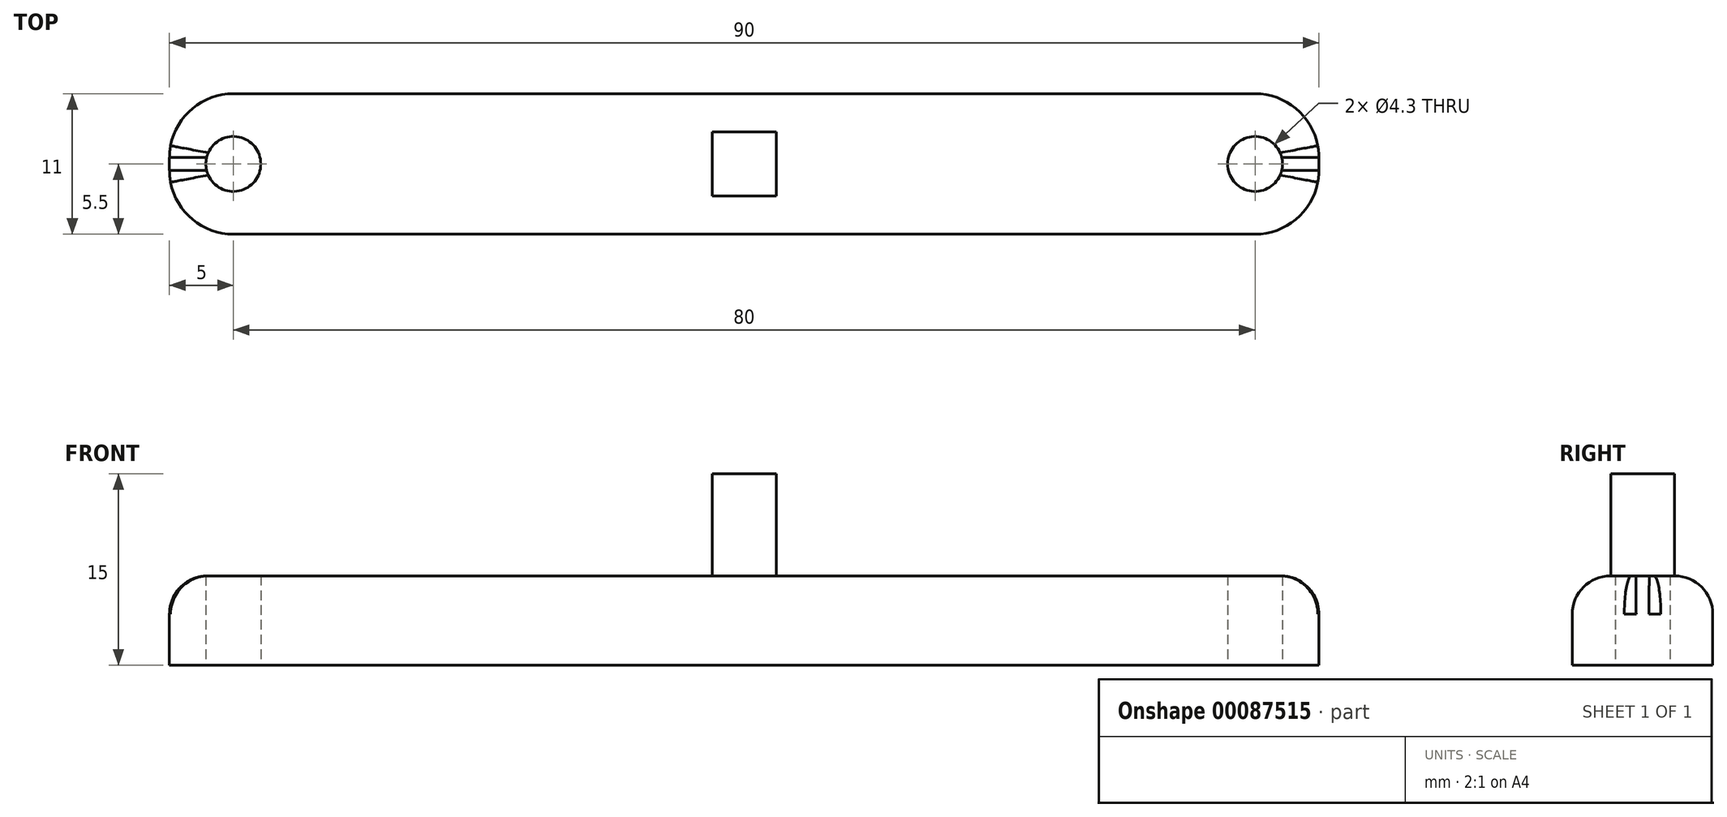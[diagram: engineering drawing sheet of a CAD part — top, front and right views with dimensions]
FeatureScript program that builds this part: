
annotation { "Feature Type Name" : "Feature", "Feature Type Description" : "" }
export const myFeature = defineFeature(function(context is Context, id is Id, definition is map)
    precondition{}
    {
        {
            var Q0;
            Q0=qCreatedBy(makeId("Top.planeOp"),FACE);
            var sketch = newSketch(context, id + "F0", { "sketchPlane" : qUnion([Q0])});
            skLineSegment(sketch, "E0.bottom", {"start": v(45, -5.5) * mm, "end": v(-45, -5.5) * mm});
            skLineSegment(sketch, "E0.top", {"start": v(45, 5.5) * mm, "end": v(-45, 5.5) * mm});
            skLineSegment(sketch, "E0.left", {"start": v(45, -5.5) * mm, "end": v(45, 5.5) * mm});
            skLineSegment(sketch, "E0.right", {"start": v(-45, -5.5) * mm, "end": v(-45, 5.5) * mm});
            skPoint(sketch, "E0.middle", {"position": v(0, 0) * mm});
            skCircle(sketch, "E1", {"center": v(0, 0) * mm, "radius": 2.25 * mm});
            skCircle(sketch, "E2", {"center": v(-40, 0) * mm, "radius": 2.15 * mm});
            skCircle(sketch, "E3", {"center": v(40, 0) * mm, "radius": 2.15 * mm});
            skSolve(sketch);
        }
        {
            var Q0;
            Q0=makeQuery(id+"F0.imprint","IMPRINT",FACE,{"disambiguationData":[TD([[makeQuery(id+"F0.imprint","IMPRINT",EDGE,{"derivedFrom":sQuery(id+"F0.wireOp",EDGE,"E0.bottom")}),-1.0]])]});
            var Q1;
            Q1=makeQuery(id+"F0.imprint","IMPRINT",FACE,{"disambiguationData":[TD([[makeQuery(id+"F0.imprint","IMPRINT",EDGE,{"derivedFrom":sQuery(id+"F0.wireOp",EDGE,"E1")}),1.0]])]});
            extrude(context, id + "F1", {"entities" : qUnion([Q0, Q1]), "depth" : 7 * mm});
        }
        {
            var Q0;
            Q0=makeQuery(id+"F1.opExtrude","CAP_FACE",FACE,{"disambiguationData":[OSD([sQuery(id+"F0.wireOp",EDGE,"E0.bottom"),sQuery(id+"F0.wireOp",EDGE,"E0.top"),sQuery(id+"F0.wireOp",EDGE,"E0.left"),sQuery(id+"F0.wireOp",EDGE,"E0.right"),sQuery(id+"F0.wireOp",EDGE,"E2"),sQuery(id+"F0.wireOp",EDGE,"E3")])],"isStart":false});
            var sketch = newSketch(context, id + "F2", { "sketchPlane" : qUnion([Q0])});
            skLineSegment(sketch, "E4.bottom", {"start": v(-2.5, 2.5) * mm, "end": v(2.5, 2.5) * mm});
            skLineSegment(sketch, "E4.top", {"start": v(-2.5, -2.5) * mm, "end": v(2.5, -2.5) * mm});
            skLineSegment(sketch, "E4.left", {"start": v(-2.5, 2.5) * mm, "end": v(-2.5, -2.5) * mm});
            skLineSegment(sketch, "E4.right", {"start": v(2.5, 2.5) * mm, "end": v(2.5, -2.5) * mm});
            skPoint(sketch, "E4.middle", {"position": v(0, 0) * mm});
            skSolve(sketch);
        }
        {
            var Q0;
            Q0=makeQuery(id+"F2.imprint","IMPRINT",FACE,{"disambiguationData":[TD([[makeQuery(id+"F2.imprint","IMPRINT",EDGE,{"derivedFrom":sQuery(id+"F2.wireOp",EDGE,"E4.bottom")}),-1.0]])]});
            extrude(context, id + "F3", {"entities" : qUnion([Q0]), "operationType" : NewBodyOperationType.ADD, "depth" : 8 * mm});
        }
        {
            var Q0;
            Q0=makeQuery(id+"F1.opExtrude","SWEPT_EDGE",EDGE,{"disambiguationData":[OSD([sQuery(id+"F0.wireOp",EDGE,"E0.bottom"),sQuery(id+"F0.wireOp",EDGE,"E0.left")])]});
            var Q1;
            Q1=makeQuery(id+"F1.opExtrude","SWEPT_EDGE",EDGE,{"disambiguationData":[OSD([sQuery(id+"F0.wireOp",EDGE,"E0.top"),sQuery(id+"F0.wireOp",EDGE,"E0.left")])]});
            var Q2;
            Q2=makeQuery(id+"F1.opExtrude","SWEPT_EDGE",EDGE,{"disambiguationData":[OSD([sQuery(id+"F0.wireOp",EDGE,"E0.bottom"),sQuery(id+"F0.wireOp",EDGE,"E0.right")])]});
            var Q3;
            Q3=makeQuery(id+"F1.opExtrude","SWEPT_EDGE",EDGE,{"disambiguationData":[OSD([sQuery(id+"F0.wireOp",EDGE,"E0.top"),sQuery(id+"F0.wireOp",EDGE,"E0.right")])]});
            fillet(context, id + "F4", {"entities" : qUnion([Q0, Q1, Q2, Q3]), "radius" : 5 * mm, "tangentPropagation" : true, "allowEdgeOverflow" : false});
        }
        {
            var Q0;
            Q0=makeQuery(id+"F1.opExtrude","CAP_EDGE",EDGE,{"disambiguationData":[OSD([sQuery(id+"F0.wireOp",EDGE,"E0.bottom")])],"isStart":false});
            fillet(context, id + "F5", {"entities" : qUnion([Q0]), "radius" : 3 * mm, "tangentPropagation" : true, "allowEdgeOverflow" : false});
        }
    });
